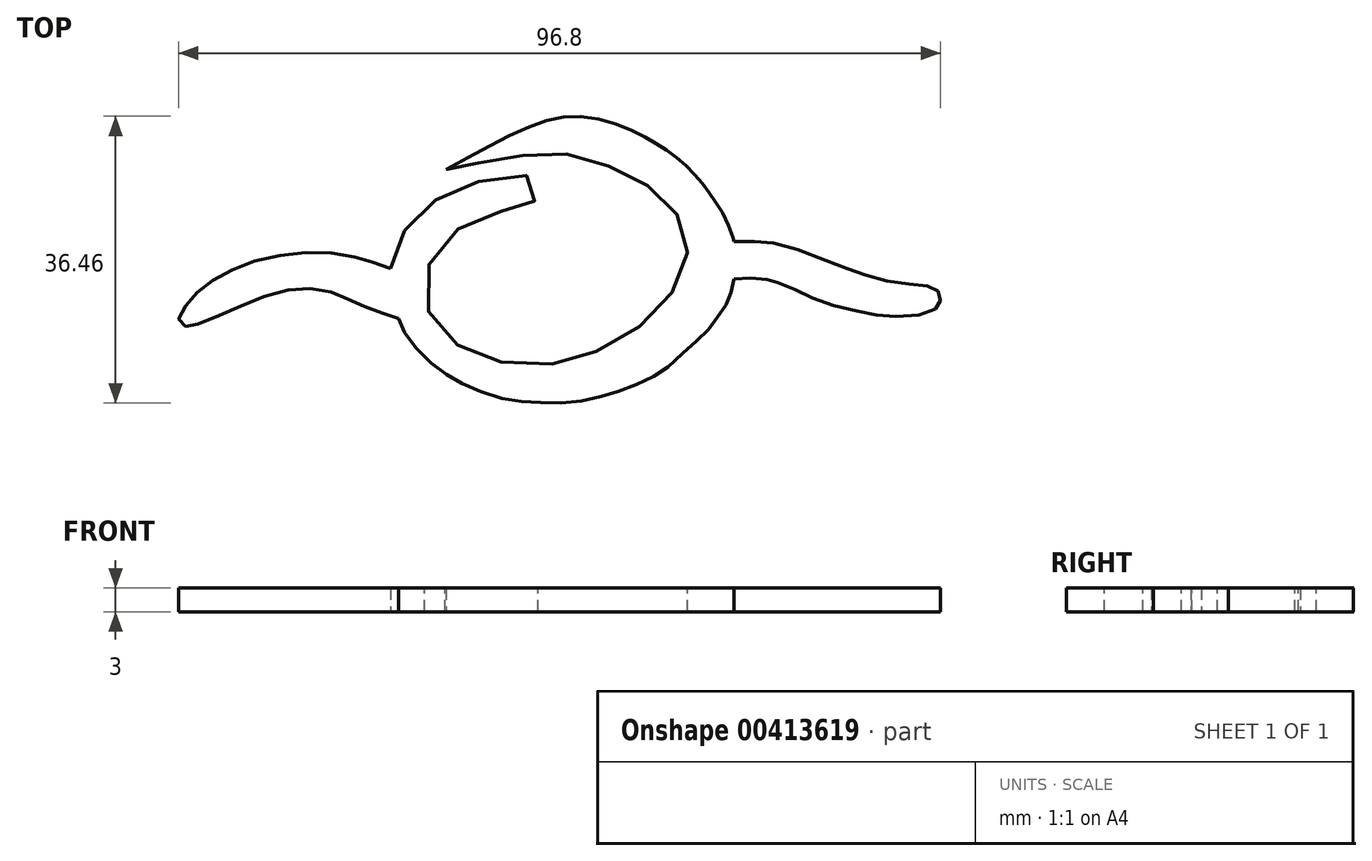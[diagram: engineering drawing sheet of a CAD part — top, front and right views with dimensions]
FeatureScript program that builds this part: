
annotation { "Feature Type Name" : "Feature", "Feature Type Description" : "" }
export const myFeature = defineFeature(function(context is Context, id is Id, definition is map)
    precondition{}
    {
        {
            var Q0;
            Q0=qCreatedBy(makeId("Top.planeOp"),FACE);
            var sketch = newSketch(context, id + "F0", { "sketchPlane" : qUnion([Q0])});
            skFitSpline(sketch, "E0", {"points": [v(-2.99, 26.66) * mm, v(7.47, 32.06) * mm, v(14.09, 33.42) * mm, v(20.66, 31.59) * mm, v(24.08, 29.71) * mm, v(26.8, 27.74) * mm, v(29.15, 25.35) * mm, v(30.8, 23.19) * mm, v(32.62, 20.14) * mm, v(33.57, 17.57) * mm, v(33.57, 17.54) * mm, v(33.57, 17.5) * mm], "startDerivative": vector(64.05, 35.74) * mm, "endDerivative": vector(3.81, -1.4) * mm});
            skFitSpline(sketch, "E1", {"points": [v(33.57, 17.5) * mm, v(36.84, 17.5) * mm, v(40.2, 16.95) * mm, v(46.43, 14.63) * mm, v(49.29, 13.58) * mm, v(53.03, 12.49) * mm, v(56.7, 12.06) * mm, v(58.84, 11.7) * mm, v(59.47, 11.23) * mm, v(59.79, 10.5) * mm, v(59.75, 9.72) * mm, v(59.25, 9) * mm, v(57.21, 8.23) * mm, v(53.12, 8.03) * mm, v(50.35, 8.44) * mm, v(46.22, 9.42) * mm, v(42.67, 10.71) * mm, v(40.15, 11.97) * mm, v(38.07, 12.6) * mm, v(37.82, 12.65) * mm, v(35.75, 12.87) * mm, v(33.57, 12.75) * mm], "startDerivative": vector(60.14, -0.44) * mm, "endDerivative": vector(-44.35, -4.96) * mm});
            skFitSpline(sketch, "E2", {"points": [v(33.57, 12.75) * mm, v(33.16, 10.94) * mm, v(32.5, 9.36) * mm, v(31.27, 7.63) * mm, v(29.87, 5.84) * mm, v(27.6, 3.8) * mm, v(24.91, 1.4) * mm, v(22.42, -0.1) * mm, v(19.03, -1.46) * mm, v(16, -2.34) * mm, v(12.07, -3) * mm, v(8.19, -2.88) * mm, v(4.72, -2.53) * mm, v(0.32, -1.12) * mm, v(-2.6, 0.37) * mm, v(-5.45, 2.61) * mm, v(-8.09, 5.58) * mm, v(-9.05, 7.75) * mm], "startDerivative": vector(-7.76, -40.75) * mm, "endDerivative": vector(-14.09, 41.08) * mm});
            skFitSpline(sketch, "E3", {"points": [v(-9.05, 7.75) * mm, v(-10.92, 8.35) * mm, v(-13.11, 9.17) * mm, v(-15.37, 10.16) * mm, v(-17.23, 10.95) * mm, v(-20.27, 11.57) * mm, v(-23.6, 11.27) * mm, v(-27.65, 9.94) * mm, v(-31.28, 8.33) * mm, v(-34.57, 7.04) * mm, v(-35.68, 6.7) * mm, v(-36.52, 6.9) * mm, v(-36.97, 7.55) * mm, v(-36.59, 8.66) * mm, v(-35.33, 10.27) * mm, v(-33.65, 11.88) * mm, v(-31, 13.5) * mm, v(-27.6, 14.95) * mm, v(-23, 15.86) * mm, v(-18.57, 16.11) * mm, v(-14.64, 15.53) * mm, v(-12.54, 14.97) * mm, v(-10.03, 14.09) * mm], "startDerivative": vector(-46.58, 14.57) * mm, "endDerivative": vector(56.75, -20.68) * mm});
            skFitSpline(sketch, "E4", {"points": [v(-10.03, 14.09) * mm, v(-9.75, 15.49) * mm, v(-8.84, 17.8) * mm, v(-7.73, 19.67) * mm, v(-6.24, 21.17) * mm, v(-4.14, 22.94) * mm, v(-2, 24.05) * mm, v(0.9, 25.08) * mm, v(4.16, 25.77) * mm, v(6.92, 25.96) * mm, v(7.99, 25.49) * mm, v(8.62, 24.52) * mm, v(8.54, 23.24) * mm, v(7.85, 22.23) * mm, v(6.82, 21.74) * mm, v(4.63, 21.39) * mm, v(2.76, 21.07) * mm, v(0.23, 20.03) * mm, v(-2.5, 18.3) * mm, v(-4.24, 16.34) * mm, v(-5.37, 14.09) * mm, v(-5.72, 11.1) * mm, v(-5.17, 8.43) * mm, v(-4.18, 6.47) * mm, v(-1.94, 4.62) * mm, v(0.17, 3.43) * mm, v(2.83, 2.45) * mm, v(6.11, 1.86) * mm, v(9.46, 1.88) * mm, v(12.3, 2.33) * mm, v(14.88, 3.12) * mm, v(16.97, 3.92) * mm, v(20.23, 5.78) * mm, v(22.22, 7.28) * mm, v(24.24, 9.36) * mm, v(26.04, 11.48) * mm, v(27.29, 13.99) * mm, v(27.61, 15.85) * mm, v(27.59, 17.65) * mm, v(26.93, 19.66) * mm, v(26.06, 21.4) * mm, v(24.58, 23.05) * mm, v(22.9, 24.42) * mm, v(21.07, 25.44) * mm, v(18.9, 26.6) * mm, v(16.51, 27.5) * mm, v(14.05, 28.2) * mm, v(12.03, 28.65) * mm, v(9.4, 28.64) * mm, v(7.16, 28.48) * mm, v(5.06, 28.24) * mm, v(2.99, 27.93) * mm, v(-1.15, 26.94) * mm, v(-2.99, 26.5) * mm, v(-3.14, 26.45) * mm, v(-3.12, 26.57) * mm, v(-2.99, 26.66) * mm], "startDerivative": vector(13.75, 90.65) * mm, "endDerivative": vector(31.68, 13.3) * mm});
            skSolve(sketch);
        }
        {
            var Q0;
            {var subQ0=sQuery(id+"F0.wireOp",EDGE,"E1");var subQ1=sQuery(id+"F0.wireOp",EDGE,"E0");var subQ2=makeQuery(id+"F0.imprint","INTERSECT",VERTEX,{"disambiguationData":[OD(0.0)],"derivedFrom":[subQ1,subQ0]});Q0=makeQuery(id+"F0.imprint","IMPRINT",FACE,{"disambiguationData":[TD([[makeQuery(id+"F0.imprint","IMPRINT",EDGE,{"disambiguationData":[TD([[subQ2,1.0]])],"derivedFrom":subQ1}),-1.0]])]});}
            extrude(context, id + "F1", {"entities" : qUnion([Q0]), "depth" : 3 * mm, "offsetDistance" : 25 * mm});
        }
    });
